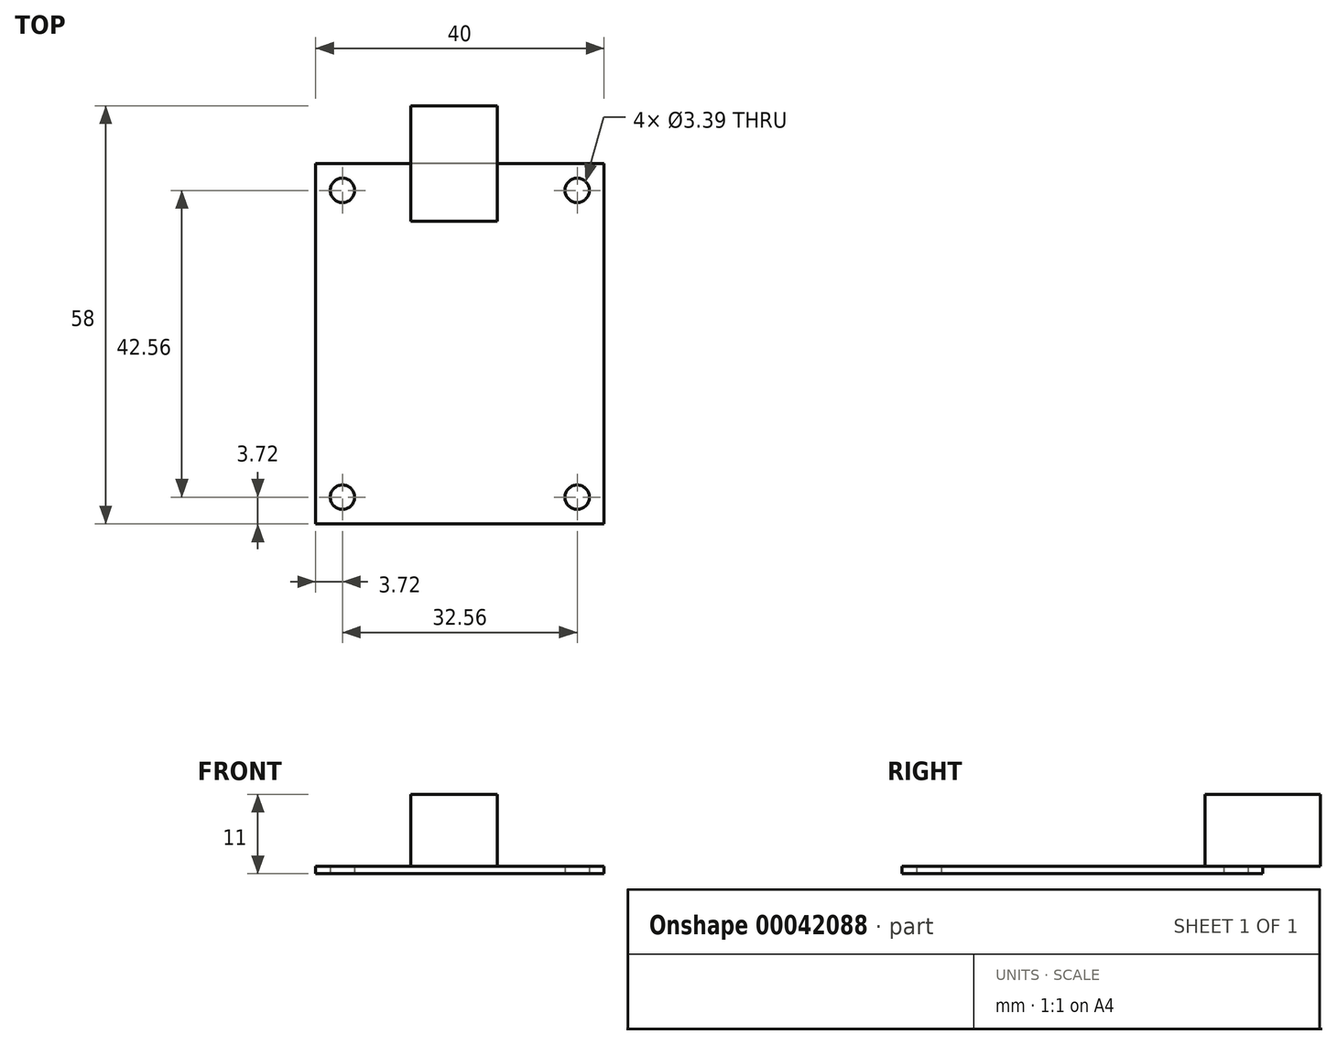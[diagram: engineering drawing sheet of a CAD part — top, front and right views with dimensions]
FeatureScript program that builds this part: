
annotation { "Feature Type Name" : "Feature", "Feature Type Description" : "" }
export const myFeature = defineFeature(function(context is Context, id is Id, definition is map)
    precondition{}
    {
        {
            var Q0;
            Q0=qCreatedBy(makeId("Top.planeOp"),FACE);
            var sketch = newSketch(context, id + "F0", { "sketchPlane" : qUnion([Q0])});
            skLineSegment(sketch, "E0.rect.bottom", {"start": v(20, -25) * mm, "end": v(-20, -25) * mm});
            skLineSegment(sketch, "E0.rect.top", {"start": v(20, 25) * mm, "end": v(-20, 25) * mm});
            skLineSegment(sketch, "E0.rect.left", {"start": v(20, -25) * mm, "end": v(20, 25) * mm});
            skLineSegment(sketch, "E0.rect.right", {"start": v(-20, -25) * mm, "end": v(-20, 25) * mm});
            skPoint(sketch, "E0.rect.middle", {"position": v(0, 0) * mm});
            skCircle(sketch, "E1", {"center": v(-16.28, 21.28) * mm, "radius": 1.7 * mm});
            skLineSegment(sketch, "E2", {"start": v(-26.55, 0) * mm, "end": v(31.37, 0) * mm, "construction": true});
            skLineSegment(sketch, "E3", {"start": v(0, -34.94) * mm, "end": v(0, 31.45) * mm, "construction": true});
            skCircle(sketch, "E4.MirrorC", {"center": v(16.28, 21.28) * mm, "radius": 1.7 * mm});
            skCircle(sketch, "E5.MirrorC", {"center": v(-16.28, -21.28) * mm, "radius": 1.7 * mm});
            skCircle(sketch, "E6.MirrorC", {"center": v(16.28, -21.28) * mm, "radius": 1.7 * mm});
            skSolve(sketch);
        }
        {
            var Q0;
            Q0 = qSketchRegion(id + "F0", true);
            extrude(context, id + "F1", {"entities" : qUnion([Q0]), "depth" : 1 * mm});
        }
        {
            var Q0;
            Q0=makeQuery(id+"F1.opExtrude","CAP_FACE",FACE,{"disambiguationData":[OSD([sQuery(id+"F0.wireOp",EDGE,"E0.rect.bottom"),sQuery(id+"F0.wireOp",EDGE,"E0.rect.top"),sQuery(id+"F0.wireOp",EDGE,"E0.rect.left"),sQuery(id+"F0.wireOp",EDGE,"E0.rect.right"),sQuery(id+"F0.wireOp",EDGE,"E1"),sQuery(id+"F0.wireOp",EDGE,"E4.MirrorC"),sQuery(id+"F0.wireOp",EDGE,"E5.MirrorC"),sQuery(id+"F0.wireOp",EDGE,"E6.MirrorC")])],"isStart":false});
            var sketch = newSketch(context, id + "F2", { "sketchPlane" : qUnion([Q0])});
            skLineSegment(sketch, "E7.bottom", {"start": v(-6.83, 33) * mm, "end": v(5.17, 33) * mm});
            skLineSegment(sketch, "E7.top", {"start": v(-6.83, 17) * mm, "end": v(5.17, 17) * mm});
            skLineSegment(sketch, "E7.left", {"start": v(-6.83, 33) * mm, "end": v(-6.83, 17) * mm});
            skLineSegment(sketch, "E7.right", {"start": v(5.17, 33) * mm, "end": v(5.17, 17) * mm});
            skSolve(sketch);
        }
        {
            var Q0;
            Q0 = qSketchRegion(id + "F2", true);
            extrude(context, id + "F3", {"entities" : qUnion([Q0]), "operationType" : NewBodyOperationType.ADD, "depth" : 10 * mm});
        }
    });
